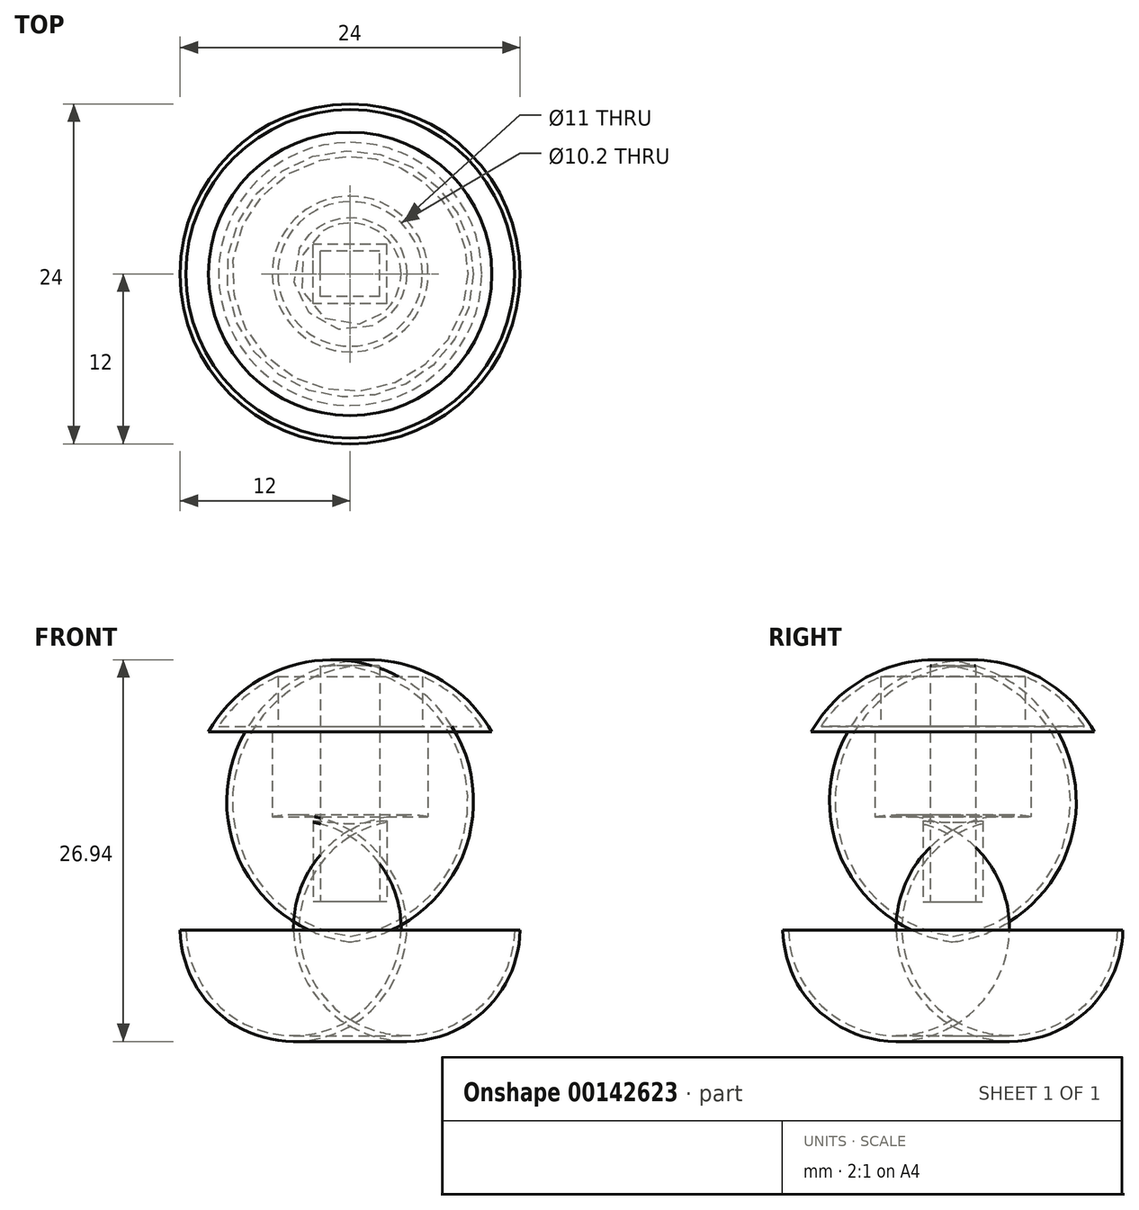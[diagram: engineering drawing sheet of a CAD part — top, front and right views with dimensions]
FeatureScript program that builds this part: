
annotation { "Feature Type Name" : "Feature", "Feature Type Description" : "" }
export const myFeature = defineFeature(function(context is Context, id is Id, definition is map)
    precondition{}
    {
        {
            var Q0;
            Q0=qCreatedBy(makeId("Front.planeOp"),FACE);
            var sketch = newSketch(context, id + "F0", { "sketchPlane" : qUnion([Q0])});
            skLineSegment(sketch, "E0", {"start": v(0, 0) * mm, "end": v(12, 0) * mm});
            skLineSegment(sketch, "E1", {"start": v(0, 0) * mm, "end": v(0, 19) * mm});
            skLineSegment(sketch, "E2", {"start": v(5.5, 8) * mm, "end": v(5.5, 14) * mm});
            skArc(sketch, "E3", {"start": v(12, 0) * mm, "mid": v(10.21, 5.19) * mm, "end": v(5.5, 8) * mm});
            skLineSegment(sketch, "E4", {"start": v(5.5, 14) * mm, "end": v(10, 14) * mm});
            skArc(sketch, "E5", {"start": v(10, 14) * mm, "mid": v(5.76, 18.03) * mm, "end": v(0, 19) * mm});
            skSolve(sketch);
        }
        {
            var Q0;
            Q0 = qSketchRegion(id + "F0", true);
            var Q1;
            Q1=sQuery(id+"F0.wireOp",EDGE,"E1");
            revolve(context, id + "F1", {"entities" : qUnion([Q0]), "axis" : qUnion([Q1]), "revolveType" : RevolveType.FULL});
        }
        {
            var Q0;
            Q0=makeQuery(id+"F1.opRevolve","SWEPT_FACE",FACE,{"disambiguationData":[OSD([sQuery(id+"F0.wireOp",EDGE,"E0")])]});
            var sketch = newSketch(context, id + "F2", { "sketchPlane" : qUnion([Q0])});
            skLineSegment(sketch, "E6.bottom", {"start": v(2.1, 1.6) * mm, "end": v(-2.1, 1.6) * mm});
            skLineSegment(sketch, "E6.top", {"start": v(2.1, -1.6) * mm, "end": v(-2.1, -1.6) * mm});
            skLineSegment(sketch, "E6.left", {"start": v(2.1, 1.6) * mm, "end": v(2.1, -1.6) * mm});
            skLineSegment(sketch, "E6.right", {"start": v(-2.1, 1.6) * mm, "end": v(-2.1, -1.6) * mm});
            skLineSegment(sketch, "E7.bottom", {"start": v(2.6, 2.1) * mm, "end": v(-2.6, 2.1) * mm});
            skLineSegment(sketch, "E7.top", {"start": v(2.6, -2.1) * mm, "end": v(-2.6, -2.1) * mm});
            skLineSegment(sketch, "E7.left", {"start": v(2.6, 2.1) * mm, "end": v(2.6, -2.1) * mm});
            skLineSegment(sketch, "E7.right", {"start": v(-2.6, 2.1) * mm, "end": v(-2.6, -2.1) * mm});
            skLineSegment(sketch, "E8", {"start": v(-2.1, 1.6) * mm, "end": v(2.1, -1.6) * mm, "construction": true});
            skLineSegment(sketch, "E9", {"start": v(-2.1, -1.6) * mm, "end": v(2.1, 1.6) * mm, "construction": true});
            skSolve(sketch);
        }
        {
            var Q0;
            Q0=makeQuery(id+"F1.opRevolve","SWEPT_FACE",FACE,{"disambiguationData":[OSD([sQuery(id+"F0.wireOp",EDGE,"E0")])]});
            shell(context, id + "F3", {"entities" : qUnion([Q0]), "thickness" : 0.4 * mm});
        }
        {
            var Q0;
            Q0 = qSketchRegion(id + "F2", true);
            var Q1;
            Q1=makeQuery(id+"F1.opRevolve","SWEPT_BODY",BODY,{"disambiguationData":[OSD([sQuery(id+"F0.wireOp",EDGE,"E0"),sQuery(id+"F0.wireOp",EDGE,"E1"),sQuery(id+"F0.wireOp",EDGE,"E2"),sQuery(id+"F0.wireOp",EDGE,"E3"),sQuery(id+"F0.wireOp",EDGE,"E4"),sQuery(id+"F0.wireOp",EDGE,"E5")])]});
            extrude(context, id + "F4", {"entities" : qUnion([Q0]), "operationType" : NewBodyOperationType.ADD, "endBound" : BoundingType.UP_TO_BODY, "oppositeDirection" : true, "endBoundEntityBody" : qUnion([Q1]), "depth" : 18.23 * mm});
        }
        {
            var Q0;
            Q0 = qSketchRegion(id + "F2", true);
            extrude(context, id + "F5", {"entities" : qUnion([Q0]), "operationType" : NewBodyOperationType.REMOVE, "oppositeDirection" : true, "depth" : 2 * mm});
        }
        {
            var Q0;
            Q0=qCreatedBy(makeId("Top.planeOp"),FACE);
            var sketch = newSketch(context, id + "F6", { "sketchPlane" : qUnion([Q0])});
            skCircle(sketch, "E10.0", {"center": v(0, 0) * mm, "radius": 5.1 * mm});
            skLineSegment(sketch, "E11.0", {"start": v(-2.6, -2.1) * mm, "end": v(-2.6, 2.1) * mm});
            skLineSegment(sketch, "E11.1", {"start": v(2.6, -2.1) * mm, "end": v(-2.6, -2.1) * mm});
            skLineSegment(sketch, "E11.2", {"start": v(2.6, -2.1) * mm, "end": v(2.6, 2.1) * mm});
            skLineSegment(sketch, "E11.3", {"start": v(2.6, 2.1) * mm, "end": v(-2.6, 2.1) * mm});
            skSolve(sketch);
        }
        {
            var Q0;
            Q0 = qSketchRegion(id + "F6", true);
            var Q1;
            Q1=makeQuery(id+"F1.opRevolve","SWEPT_BODY",BODY,{"disambiguationData":[OSD([sQuery(id+"F0.wireOp",EDGE,"E0"),sQuery(id+"F0.wireOp",EDGE,"E1"),sQuery(id+"F0.wireOp",EDGE,"E2"),sQuery(id+"F0.wireOp",EDGE,"E3"),sQuery(id+"F0.wireOp",EDGE,"E4"),sQuery(id+"F0.wireOp",EDGE,"E5")])]});
            extrude(context, id + "F7", {"entities" : qUnion([Q0]), "operationType" : NewBodyOperationType.ADD, "endBound" : BoundingType.UP_TO_BODY, "endBoundEntityBody" : qUnion([Q1]), "depth" : 25 * mm});
        }
        {
            var Q0;
            Q0 = qSketchRegion(id + "F6", true);
            var Q1;
            Q1=makeQuery(id+"F3.opShell","OFFSET_FACE",FACE,{"disambiguationData":[OSD([sQuery(id+"F0.wireOp",EDGE,"E3")])]});
            extrude(context, id + "F8", {"entities" : qUnion([Q0]), "operationType" : NewBodyOperationType.REMOVE, "endBound" : BoundingType.UP_TO_SURFACE, "endBoundEntityFace" : qUnion([Q1]), "depth" : 10 * mm});
        }
    });
